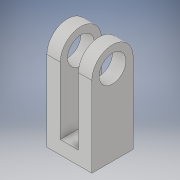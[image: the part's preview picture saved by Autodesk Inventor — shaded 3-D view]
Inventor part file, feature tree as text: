
AUTODESK INVENTOR PART (.ipt)
format: ipt  version: 2017 (Build 210142000, 142)  size: 124,416 bytes
history: native  units: in
note: dims shown in document units (in); Inventor stores cm internally (conversion verified against a paired STEP export)
features: extrude x2, sketch x2, projected_geometry x2
ambient origin geometry x8: Origin, YZ Plane, XZ Plane, XY Plane, X Axis, Y Axis, Z Axis, Center Point
bodies: Solid1 (feature_tree)
feature tree (6):
  extrude  "Extrusion1"  Depth=0.84in TaperAngle=0.0deg
  extrude  "Extrusion2"  Depth=0.25in
  sketch  "Sketch1"  dims[d0=0.5in d1=0.77in d2=1.5in d3=0.77in d4=0.84in d5=0.0in]
  sketch  "Sketch2"  dims[d6=1.635in d7=0.25in d8=0.25in d9=0.84in d10=0.0in]
  projected_geometry  "Projected Loop1"
  projected_geometry  "Projected Loop2"
